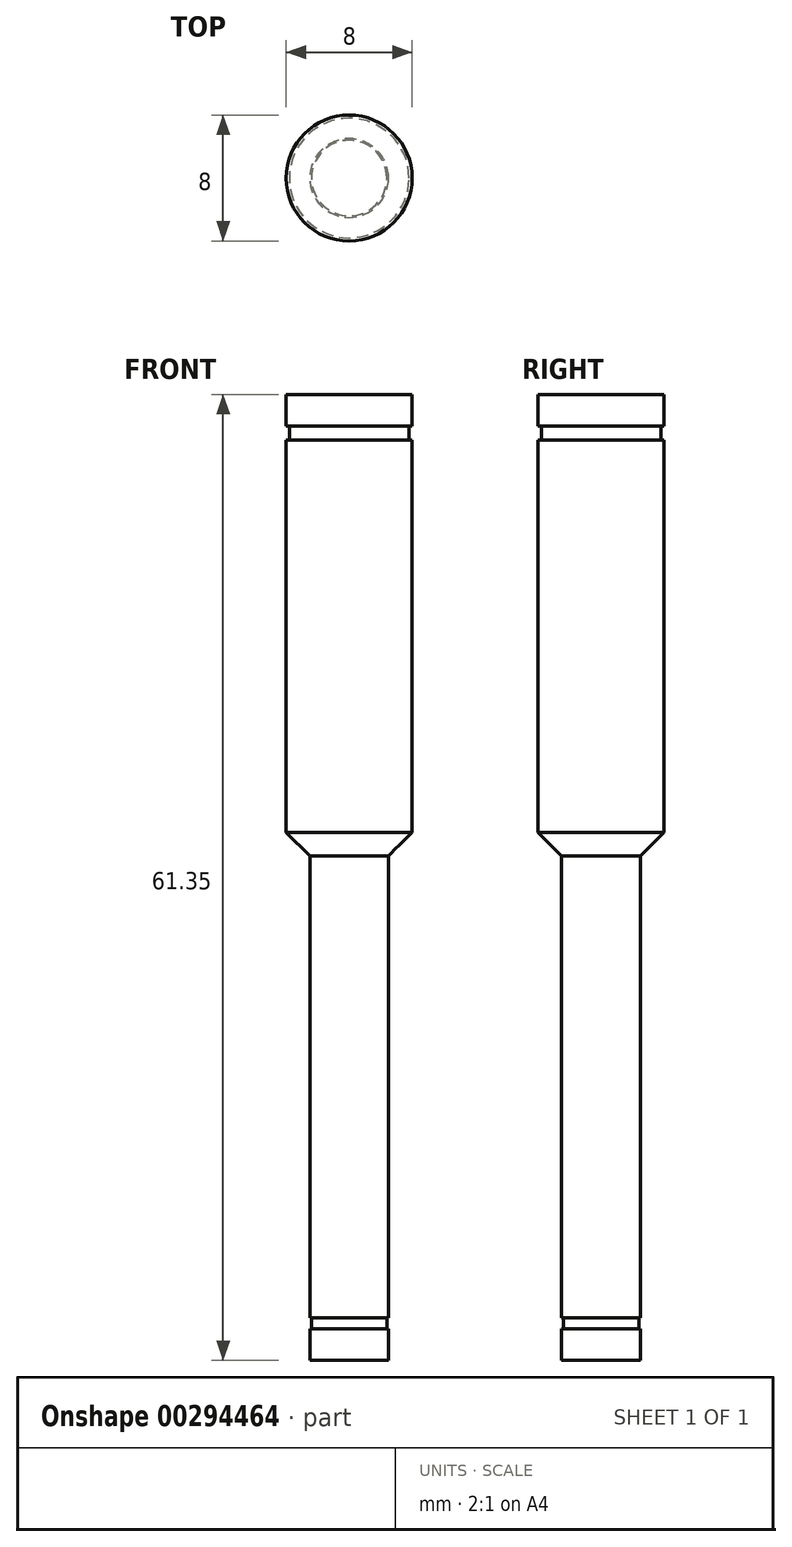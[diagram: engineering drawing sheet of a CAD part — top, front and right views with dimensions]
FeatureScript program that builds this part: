
annotation { "Feature Type Name" : "Feature", "Feature Type Description" : "" }
export const myFeature = defineFeature(function(context is Context, id is Id, definition is map)
    precondition{}
    {
        {
            var Q0;
            Q0=qCreatedBy(makeId("Top.planeOp"),FACE);
            var sketch = newSketch(context, id + "F0", { "sketchPlane" : qUnion([Q0])});
            skCircle(sketch, "E0", {"center": v(0, 0) * mm, "radius": 4 * mm});
            skSolve(sketch);
        }
        {
            var Q0;
            Q0 = qSketchRegion(id + "F0", true);
            extrude(context, id + "F1", {"entities" : qUnion([Q0]), "depth" : 200 * mm});
        }
        {
            var Q0;
            Q0=qCreatedBy(makeId("Front.planeOp"),FACE);
            var sketch = newSketch(context, id + "F2", { "sketchPlane" : qUnion([Q0])});
            skLineSegment(sketch, "E1", {"start": v(0, 0) * mm, "end": v(2.5, 0) * mm});
            skLineSegment(sketch, "E2", {"start": v(2.5, 0) * mm, "end": v(2.5, 2) * mm});
            skLineSegment(sketch, "E3", {"start": v(2.5, 2) * mm, "end": v(2.4, 2) * mm});
            skLineSegment(sketch, "E4", {"start": v(2.4, 2) * mm, "end": v(2.4, 2.7) * mm});
            skLineSegment(sketch, "E5", {"start": v(2.4, 2.7) * mm, "end": v(2.5, 2.7) * mm});
            skLineSegment(sketch, "E6", {"start": v(2.5, 2.7) * mm, "end": v(2.5, 32.05) * mm});
            skLineSegment(sketch, "E7", {"start": v(2.5, 32.05) * mm, "end": v(4, 33.55) * mm});
            skLineSegment(sketch, "E8", {"start": v(4, 33.55) * mm, "end": v(4, 0) * mm});
            skLineSegment(sketch, "E9", {"start": v(4, 0) * mm, "end": v(2.5, 0) * mm});
            skLineSegment(sketch, "E10", {"start": v(0, 0) * mm, "end": v(0, 32.05) * mm, "construction": true});
            skSolve(sketch);
        }
        {
            var Q0;
            Q0 = qSketchRegion(id + "F2", true);
            var Q1;
            Q1=sQuery(id+"F2.wireOp",EDGE,"E10");
            revolve(context, id + "F3", {"operationType" : NewBodyOperationType.REMOVE, "entities" : qUnion([Q0]), "axis" : qUnion([Q1]), "revolveType" : RevolveType.FULL, "oppositeDirection" : true});
        }
        {
            var Q0;
            Q0=qCreatedBy(makeId("Front.planeOp"),FACE);
            var sketch = newSketch(context, id + "F4", { "sketchPlane" : qUnion([Q0])});
            skLineSegment(sketch, "E11.bottom", {"start": v(0, 61.35) * mm, "end": v(4, 61.35) * mm});
            skLineSegment(sketch, "E11.top", {"start": v(0, 200) * mm, "end": v(4, 200) * mm});
            skLineSegment(sketch, "E11.left", {"start": v(0, 61.35) * mm, "end": v(0, 200) * mm});
            skLineSegment(sketch, "E11.right", {"start": v(4, 63.53) * mm, "end": v(4, 200) * mm});
            skLineSegment(sketch, "E12", {"start": v(4, 61.35) * mm, "end": v(4, 59.35) * mm});
            skLineSegment(sketch, "E13", {"start": v(4, 59.35) * mm, "end": v(3.8, 59.35) * mm});
            skLineSegment(sketch, "E14", {"start": v(3.8, 59.35) * mm, "end": v(3.8, 58.45) * mm});
            skLineSegment(sketch, "E15", {"start": v(3.8, 58.45) * mm, "end": v(4, 58.45) * mm});
            skLineSegment(sketch, "E16", {"start": v(4, 58.45) * mm, "end": v(6.54, 58.45) * mm});
            skLineSegment(sketch, "E17", {"start": v(6.54, 58.45) * mm, "end": v(6.54, 63.53) * mm});
            skLineSegment(sketch, "E18", {"start": v(6.54, 63.53) * mm, "end": v(4, 63.53) * mm});
            skSolve(sketch);
        }
        {
            var Q0;
            Q0=makeQuery(id+"F4.imprint","IMPRINT",FACE,{"disambiguationData":[TD([[makeQuery(id+"F4.imprint","IMPRINT",EDGE,{"derivedFrom":sQuery(id+"F4.wireOp",EDGE,"E11.bottom")}),1.0]])]});
            var Q1;
            Q1=sQuery(id+"F4.wireOp",EDGE,"E11.left");
            revolve(context, id + "F5", {"operationType" : NewBodyOperationType.REMOVE, "entities" : qUnion([Q0]), "axis" : qUnion([Q1]), "revolveType" : RevolveType.FULL, "oppositeDirection" : true});
        }
    });
